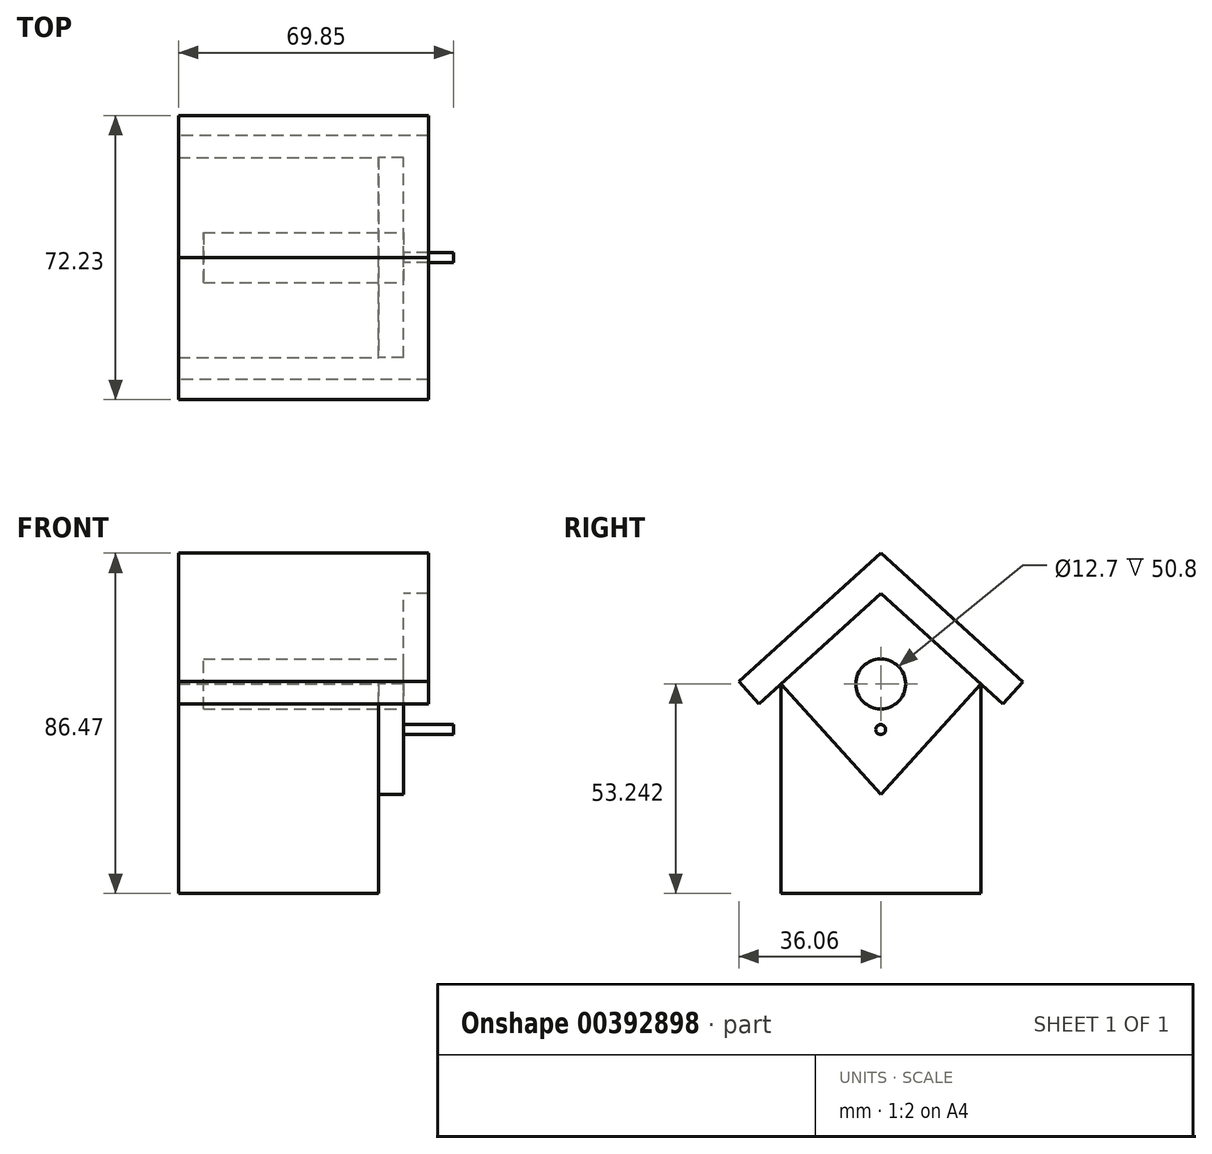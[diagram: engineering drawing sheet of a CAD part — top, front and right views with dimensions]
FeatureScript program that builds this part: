
annotation { "Feature Type Name" : "Feature", "Feature Type Description" : "" }
export const myFeature = defineFeature(function(context is Context, id is Id, definition is map)
    precondition{}
    {
        {
            var Q0;
            Q0=qCreatedBy(makeId("Top.planeOp"),FACE);
            var sketch = newSketch(context, id + "F0", { "sketchPlane" : qUnion([Q0])});
            skLineSegment(sketch, "E0.bottom", {"start": v(-25.4, 25.4) * mm, "end": v(25.4, 25.4) * mm});
            skLineSegment(sketch, "E0.top", {"start": v(-25.4, -25.4) * mm, "end": v(25.4, -25.4) * mm});
            skLineSegment(sketch, "E0.left", {"start": v(-25.4, 25.4) * mm, "end": v(-25.4, -25.4) * mm});
            skLineSegment(sketch, "E0.right", {"start": v(25.4, 25.4) * mm, "end": v(25.4, -25.4) * mm});
            skPoint(sketch, "E0.middle", {"position": v(0, 0) * mm});
            skSolve(sketch);
        }
        {
            var Q0;
            Q0=makeQuery(id+"F0.imprint","IMPRINT",FACE,{"disambiguationData":[TD([[makeQuery(id+"F0.imprint","IMPRINT",EDGE,{"derivedFrom":sQuery(id+"F0.wireOp",EDGE,"E0.bottom")}),-1.0]])]});
            extrude(context, id + "F1", {"entities" : qUnion([Q0]), "depth" : 63.5 * mm});
        }
        {
            var Q0;
            Q0=makeQuery(id+"F1.opExtrude","SWEPT_FACE",FACE,{"disambiguationData":[OSD([sQuery(id+"F0.wireOp",EDGE,"E0.right")])]});
            var sketch = newSketch(context, id + "F2", { "sketchPlane" : qUnion([Q0])});
            skLineSegment(sketch, "E1", {"start": v(0, 76.2) * mm, "end": v(0, 86.47) * mm});
            skPoint(sketch, "E1.endSnap0", {"position": v(0, 63.5) * mm});
            skLineSegment(sketch, "E2", {"start": v(-25.34, 52.79) * mm, "end": v(-25.27, 52.85) * mm});
            skLineSegment(sketch, "E3", {"start": v(-30.96, 48.22) * mm, "end": v(0, 76.2) * mm});
            skLineSegment(sketch, "E4", {"start": v(0, 76.2) * mm, "end": v(31.06, 48.12) * mm});
            skLineSegment(sketch, "E5", {"start": v(-25.4, 52.85) * mm, "end": v(0, 27.45) * mm});
            skLineSegment(sketch, "E6", {"start": v(0, 27.45) * mm, "end": v(25.4, 52.85) * mm});
            skLineSegment(sketch, "E7", {"start": v(-30.96, 48.22) * mm, "end": v(-36.06, 53.87) * mm});
            skLineSegment(sketch, "E8", {"start": v(31.06, 48.12) * mm, "end": v(36.17, 53.78) * mm});
            skLineSegment(sketch, "E9", {"start": v(-36.06, 53.87) * mm, "end": v(0, 86.47) * mm});
            skLineSegment(sketch, "E10", {"start": v(0, 86.47) * mm, "end": v(36.17, 53.78) * mm});
            skSolve(sketch);
        }
        {
            var Q0;
            {var subQ1=sQuery(id+"F2.wireOp",EDGE,"E1");Q0=makeQuery(id+"F2.imprint","IMPRINT",FACE,{"disambiguationData":[TD([[makeQuery(id+"F2.imprint","IMPRINT",EDGE,{"derivedFrom":subQ1}),1.0]])]});}
            var Q1;
            {var subQ0=sQuery(id+"F2.wireOp",EDGE,"E3");var subQ1=sQuery(id+"F0.wireOp",EDGE,"E0.right");var subQ4=makeQuery(id+"F1.opExtrude","CAP_EDGE",EDGE,{"disambiguationData":[OSD([subQ1])],"isStart":false});var subQ5=makeQuery(id+"F2.imprint","INTERSECT",VERTEX,{"derivedFrom":[subQ4,subQ0]});Q1=makeQuery(id+"F2.imprint","IMPRINT",FACE,{"disambiguationData":[TD([[makeQuery(id+"F2.imprint","IMPRINT",EDGE,{"disambiguationData":[TD([[subQ5,1.0]])],"derivedFrom":subQ0}),1.0]])]});}
            var Q2;
            {var subQ1=sQuery(id+"F2.wireOp",EDGE,"E1");Q2=makeQuery(id+"F2.imprint","IMPRINT",FACE,{"disambiguationData":[TD([[makeQuery(id+"F2.imprint","IMPRINT",EDGE,{"derivedFrom":subQ1}),-1.0]])]});}
            var Q3;
            {var subQ0=sQuery(id+"F2.wireOp",EDGE,"E4");var subQ1=sQuery(id+"F0.wireOp",EDGE,"E0.right");var subQ4=makeQuery(id+"F1.opExtrude","CAP_EDGE",EDGE,{"disambiguationData":[OSD([subQ1])],"isStart":false});var subQ5=makeQuery(id+"F2.imprint","INTERSECT",VERTEX,{"derivedFrom":[subQ4,subQ0]});Q3=makeQuery(id+"F2.imprint","IMPRINT",FACE,{"disambiguationData":[TD([[makeQuery(id+"F2.imprint","IMPRINT",EDGE,{"disambiguationData":[TD([[subQ5,-1.0]])],"derivedFrom":subQ0}),1.0]])]});}
            extrude(context, id + "F3", {"entities" : qUnion([Q0, Q1, Q2, Q3]), "operationType" : NewBodyOperationType.ADD, "depth" : 12.7 * mm});
        }
        {
            var Q0;
            Q0=makeQuery(id+"F1.opExtrude","SWEPT_FACE",FACE,{"disambiguationData":[OSD([sQuery(id+"F0.wireOp",EDGE,"E0.right")])]});
            var sketch = newSketch(context, id + "F4", { "sketchPlane" : qUnion([Q0])});
            skLineSegment(sketch, "E11", {"start": v(-25.4, 53.24) * mm, "end": v(0, 25.14) * mm});
            skLineSegment(sketch, "E12", {"start": v(0, 25.14) * mm, "end": v(25.4, 53.24) * mm});
            skLineSegment(sketch, "E13", {"start": v(-14.05, 63.5) * mm, "end": v(0, 76.2) * mm});
            skLineSegment(sketch, "E14", {"start": v(0, 76.2) * mm, "end": v(14.05, 63.5) * mm});
            skSolve(sketch);
        }
        {
            var Q0;
            Q0=makeQuery(id+"F4.imprint","IMPRINT",FACE,{"disambiguationData":[TD([[makeQuery(id+"F4.imprint","IMPRINT",EDGE,{"derivedFrom":sQuery(id+"F4.wireOp",EDGE,"E11")}),1.0]])]});
            var Q1;
            Q1=makeQuery(id+"F4.imprint","IMPRINT",FACE,{"disambiguationData":[TD([[makeQuery(id+"F4.imprint","IMPRINT",EDGE,{"derivedFrom":sQuery(id+"F4.wireOp",EDGE,"E13")}),-1.0]])]});
            extrude(context, id + "F5", {"entities" : qUnion([Q0, Q1]), "operationType" : NewBodyOperationType.ADD, "depth" : 6.35 * mm});
        }
        {
            var Q0;
            {var subQ0=sQuery(id+"F2.wireOp",EDGE,"E4");var subQ1=sQuery(id+"F2.wireOp",EDGE,"E3");var subQ2=sQuery(id+"F0.wireOp",EDGE,"E0.top");var subQ3=sQuery(id+"F0.wireOp",EDGE,"E0.right");var subQ4=sQuery(id+"F0.wireOp",EDGE,"E0.bottom");var subQ5=sQuery(id+"F2.wireOp",EDGE,"E10");var subQ6=sQuery(id+"F2.wireOp",EDGE,"E9");var subQ7=makeQuery(id+"F3.opExtrude","CAP_FACE",FACE,{"disambiguationData":[OSD([subQ1,subQ0,sQuery(id+"F2.wireOp",EDGE,"E7"),sQuery(id+"F2.wireOp",EDGE,"E8"),subQ6,subQ5])],"isStart":true});Q0=makeQuery(id+"F5.boolean.opBoolean","MERGE",FACE,{"derivedFrom":[makeQuery(id+"F3.boolean.opBoolean","SPLIT",FACE,{"disambiguationData":[TD([makeQuery(id+"F1.opExtrude","SWEPT_FACE",FACE,{"disambiguationData":[OSD([subQ4])]}),makeQuery(id+"F1.opExtrude","CAP_FACE",FACE,{"disambiguationData":[OSD([subQ4,subQ2,sQuery(id+"F0.wireOp",EDGE,"E0.left"),subQ3])],"isStart":false}),makeQuery(id+"F1.opExtrude","SWEPT_FACE",FACE,{"disambiguationData":[OSD([subQ2])]}),makeQuery(id+"F1.opExtrude","SWEPT_FACE",FACE,{"disambiguationData":[OSD([subQ3])]}),makeQuery(id+"F3.opExtrude","SWEPT_FACE",FACE,{"disambiguationData":[OSD([subQ1])]}),subQ7,makeQuery(id+"F3.opExtrude","SWEPT_FACE",FACE,{"disambiguationData":[OSD([subQ0])]}),makeQuery(id+"F3.opExtrude","SWEPT_FACE",FACE,{"disambiguationData":[OSD([subQ6])]}),makeQuery(id+"F3.opExtrude","SWEPT_FACE",FACE,{"disambiguationData":[OSD([subQ5])]})])],"derivedFrom":subQ7}),makeQuery(id+"F5.opExtrude","CAP_FACE",FACE,{"disambiguationData":[OSD([subQ1,subQ0,sQuery(id+"F4.wireOp",EDGE,"E11"),sQuery(id+"F4.wireOp",EDGE,"E12"),sQuery(id+"F4.wireOp",EDGE,"E13"),sQuery(id+"F4.wireOp",EDGE,"E14")])],"isStart":true})]});}
            var Q1;
            {var subQ0=sQuery(id+"F2.wireOp",EDGE,"E10");var subQ1=sQuery(id+"F2.wireOp",EDGE,"E8");var subQ2=sQuery(id+"F2.wireOp",EDGE,"E4");var subQ3=makeQuery(id+"F3.opExtrude","CAP_FACE",FACE,{"disambiguationData":[OSD([sQuery(id+"F2.wireOp",EDGE,"E3"),subQ2,sQuery(id+"F2.wireOp",EDGE,"E7"),subQ1,sQuery(id+"F2.wireOp",EDGE,"E9"),subQ0])],"isStart":true});var subQ4=sQuery(id+"F0.wireOp",EDGE,"E0.right");var subQ5=sQuery(id+"F0.wireOp",EDGE,"E0.bottom");Q1=makeQuery(id+"F3.boolean.opBoolean","SPLIT",FACE,{"disambiguationData":[TD([makeQuery(id+"F1.opExtrude","SWEPT_FACE",FACE,{"disambiguationData":[OSD([subQ5])]}),makeQuery(id+"F1.opExtrude","CAP_FACE",FACE,{"disambiguationData":[OSD([subQ5,sQuery(id+"F0.wireOp",EDGE,"E0.top"),sQuery(id+"F0.wireOp",EDGE,"E0.left"),subQ4])],"isStart":false}),makeQuery(id+"F1.opExtrude","SWEPT_FACE",FACE,{"disambiguationData":[OSD([subQ4])]}),subQ3,makeQuery(id+"F3.opExtrude","SWEPT_FACE",FACE,{"disambiguationData":[OSD([subQ2])]}),makeQuery(id+"F3.opExtrude","SWEPT_FACE",FACE,{"disambiguationData":[OSD([subQ1])]}),makeQuery(id+"F3.opExtrude","SWEPT_FACE",FACE,{"disambiguationData":[OSD([subQ0])]})])],"derivedFrom":subQ3});}
            var Q2;
            {var subQ0=sQuery(id+"F0.wireOp",EDGE,"E0.right");var subQ1=sQuery(id+"F2.wireOp",EDGE,"E7");var subQ2=sQuery(id+"F2.wireOp",EDGE,"E3");var subQ3=sQuery(id+"F0.wireOp",EDGE,"E0.top");var subQ4=sQuery(id+"F2.wireOp",EDGE,"E9");var subQ5=makeQuery(id+"F3.opExtrude","CAP_FACE",FACE,{"disambiguationData":[OSD([subQ2,sQuery(id+"F2.wireOp",EDGE,"E4"),subQ1,sQuery(id+"F2.wireOp",EDGE,"E8"),subQ4,sQuery(id+"F2.wireOp",EDGE,"E10")])],"isStart":true});Q2=makeQuery(id+"F3.boolean.opBoolean","SPLIT",FACE,{"disambiguationData":[TD([makeQuery(id+"F1.opExtrude","CAP_FACE",FACE,{"disambiguationData":[OSD([sQuery(id+"F0.wireOp",EDGE,"E0.bottom"),subQ3,sQuery(id+"F0.wireOp",EDGE,"E0.left"),subQ0])],"isStart":false}),makeQuery(id+"F1.opExtrude","SWEPT_FACE",FACE,{"disambiguationData":[OSD([subQ3])]}),makeQuery(id+"F1.opExtrude","SWEPT_FACE",FACE,{"disambiguationData":[OSD([subQ0])]}),makeQuery(id+"F3.opExtrude","SWEPT_FACE",FACE,{"disambiguationData":[OSD([subQ2])]}),subQ5,makeQuery(id+"F3.opExtrude","SWEPT_FACE",FACE,{"disambiguationData":[OSD([subQ1])]}),makeQuery(id+"F3.opExtrude","SWEPT_FACE",FACE,{"disambiguationData":[OSD([subQ4])]})])],"derivedFrom":subQ5});}
            extrude(context, id + "F6", {"entities" : qUnion([Q0, Q1, Q2]), "operationType" : NewBodyOperationType.ADD, "depth" : 50.8 * mm});
        }
        {
            var Q0;
            Q0=makeQuery(id+"F5.opExtrude","CAP_FACE",FACE,{"disambiguationData":[OSD([sQuery(id+"F2.wireOp",EDGE,"E3"),sQuery(id+"F2.wireOp",EDGE,"E4"),sQuery(id+"F4.wireOp",EDGE,"E11"),sQuery(id+"F4.wireOp",EDGE,"E12"),sQuery(id+"F4.wireOp",EDGE,"E13"),sQuery(id+"F4.wireOp",EDGE,"E14")])],"isStart":false});
            var sketch = newSketch(context, id + "F7", { "sketchPlane" : qUnion([Q0])});
            skLineSegment(sketch, "E15", {"start": v(-25.4, 53.24) * mm, "end": v(25.4, 53.24) * mm});
            skCircle(sketch, "E16", {"center": v(0, 53.24) * mm, "radius": 6.35 * mm});
            skSolve(sketch);
        }
        {
            var Q0;
            {var subQ0=sQuery(id+"F7.wireOp",EDGE,"E16");var subQ1=sQuery(id+"F7.wireOp",EDGE,"E15");var subQ2=makeQuery(id+"F7.imprint","INTERSECT",VERTEX,{"disambiguationData":[OD(0.0)],"derivedFrom":[subQ1,subQ0]});Q0=makeQuery(id+"F7.imprint","IMPRINT",FACE,{"disambiguationData":[TD([[makeQuery(id+"F7.imprint","IMPRINT",EDGE,{"disambiguationData":[TD([[subQ2,-1.0]])],"derivedFrom":subQ1}),1.0]])]});}
            var Q1;
            {var subQ0=sQuery(id+"F7.wireOp",EDGE,"E16");var subQ1=sQuery(id+"F7.wireOp",EDGE,"E15");var subQ2=makeQuery(id+"F7.imprint","INTERSECT",VERTEX,{"disambiguationData":[OD(0.0)],"derivedFrom":[subQ1,subQ0]});Q1=makeQuery(id+"F7.imprint","IMPRINT",FACE,{"disambiguationData":[TD([[makeQuery(id+"F7.imprint","IMPRINT",EDGE,{"disambiguationData":[TD([[subQ2,-1.0]])],"derivedFrom":subQ1}),-1.0]])]});}
            extrude(context, id + "F8", {"entities" : qUnion([Q0, Q1]), "operationType" : NewBodyOperationType.REMOVE, "oppositeDirection" : true, "depth" : 50.8 * mm});
        }
        {
            var Q0;
            Q0=makeQuery(id+"F5.opExtrude","CAP_FACE",FACE,{"disambiguationData":[OSD([sQuery(id+"F2.wireOp",EDGE,"E3"),sQuery(id+"F2.wireOp",EDGE,"E4"),sQuery(id+"F4.wireOp",EDGE,"E11"),sQuery(id+"F4.wireOp",EDGE,"E12"),sQuery(id+"F4.wireOp",EDGE,"E13"),sQuery(id+"F4.wireOp",EDGE,"E14")])],"isStart":false});
            var sketch = newSketch(context, id + "F9", { "sketchPlane" : qUnion([Q0])});
            skLineSegment(sketch, "E17", {"start": v(0, 25.14) * mm, "end": v(0, 41.65) * mm});
            skCircle(sketch, "E18", {"center": v(0, 41.65) * mm, "radius": 1.27 * mm});
            skSolve(sketch);
        }
        {
            var Q0;
            Q0=makeQuery(id+"F9.imprint","IMPRINT",FACE,{"disambiguationData":[TD([[makeQuery(id+"F9.imprint","IMPRINT",EDGE,{"derivedFrom":sQuery(id+"F9.wireOp",EDGE,"E18")}),1.0]])]});
            extrude(context, id + "F10", {"entities" : qUnion([Q0]), "operationType" : NewBodyOperationType.ADD, "depth" : 12.7 * mm});
        }
    });
